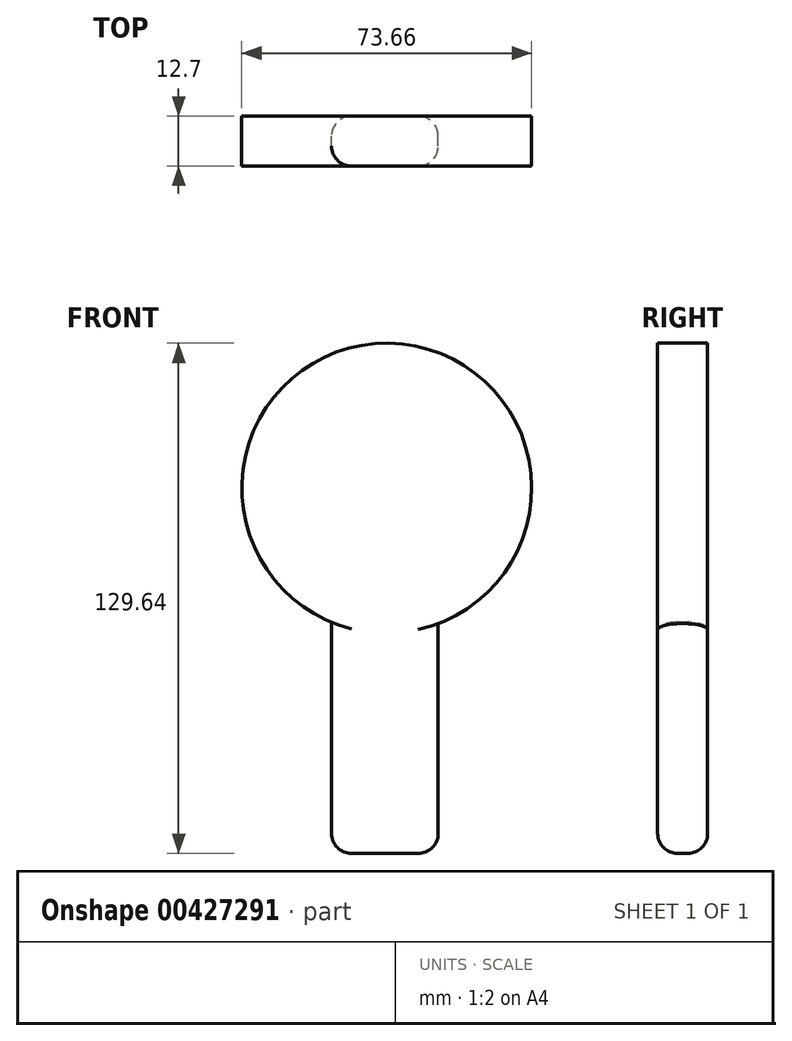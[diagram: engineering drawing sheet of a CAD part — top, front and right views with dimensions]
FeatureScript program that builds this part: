
annotation { "Feature Type Name" : "Feature", "Feature Type Description" : "" }
export const myFeature = defineFeature(function(context is Context, id is Id, definition is map)
    precondition{}
    {
        {
            var Q0;
            Q0=qCreatedBy(makeId("Front.planeOp"),FACE);
            var sketch = newSketch(context, id + "F0", { "sketchPlane" : qUnion([Q0])});
            skCircle(sketch, "E0", {"center": v(0, 36.75) * mm, "radius": 36.83 * mm});
            skLineSegment(sketch, "E1.bottom", {"start": v(-14.05, 2.7) * mm, "end": v(13.06, 2.7) * mm});
            skLineSegment(sketch, "E1.top", {"start": v(-14.05, -56.06) * mm, "end": v(13.06, -56.06) * mm});
            skLineSegment(sketch, "E1.left", {"start": v(-14.05, 2.7) * mm, "end": v(-14.05, -56.06) * mm});
            skLineSegment(sketch, "E1.right", {"start": v(13.06, 2.7) * mm, "end": v(13.06, -56.06) * mm});
            skSolve(sketch);
        }
        {
            var Q0;
            Q0 = qSketchRegion(id + "F0", true);
            extrude(context, id + "F1", {"entities" : qUnion([Q0]), "depth" : 12.7 * mm});
        }
        {
            var Q0;
            Q0=makeQuery(id+"F1.opExtrude","CAP_EDGE",EDGE,{"disambiguationData":[OSD([sQuery(id+"F0.wireOp",EDGE,"E1.left")])],"isStart":false});
            var Q1;
            Q1=makeQuery(id+"F1.opExtrude","CAP_EDGE",EDGE,{"disambiguationData":[OSD([sQuery(id+"F0.wireOp",EDGE,"E1.left")])],"isStart":true});
            var Q2;
            Q2=makeQuery(id+"F1.opExtrude","CAP_EDGE",EDGE,{"disambiguationData":[OSD([sQuery(id+"F0.wireOp",EDGE,"E1.top")])],"isStart":false});
            var Q3;
            Q3=makeQuery(id+"F1.opExtrude","CAP_EDGE",EDGE,{"disambiguationData":[OSD([sQuery(id+"F0.wireOp",EDGE,"E1.right")])],"isStart":false});
            var Q4;
            Q4=makeQuery(id+"F1.opExtrude","CAP_EDGE",EDGE,{"disambiguationData":[OSD([sQuery(id+"F0.wireOp",EDGE,"E1.right")])],"isStart":true});
            var Q5;
            Q5=makeQuery(id+"F1.opExtrude","SWEPT_FACE",FACE,{"disambiguationData":[OSD([sQuery(id+"F0.wireOp",EDGE,"E1.top")])]});
            fillet(context, id + "F2", {"entities" : qUnion([Q0, Q1, Q2, Q3, Q4, Q5]), "radius" : 5.08 * mm, "tangentPropagation" : true, "allowEdgeOverflow" : false});
        }
    });
